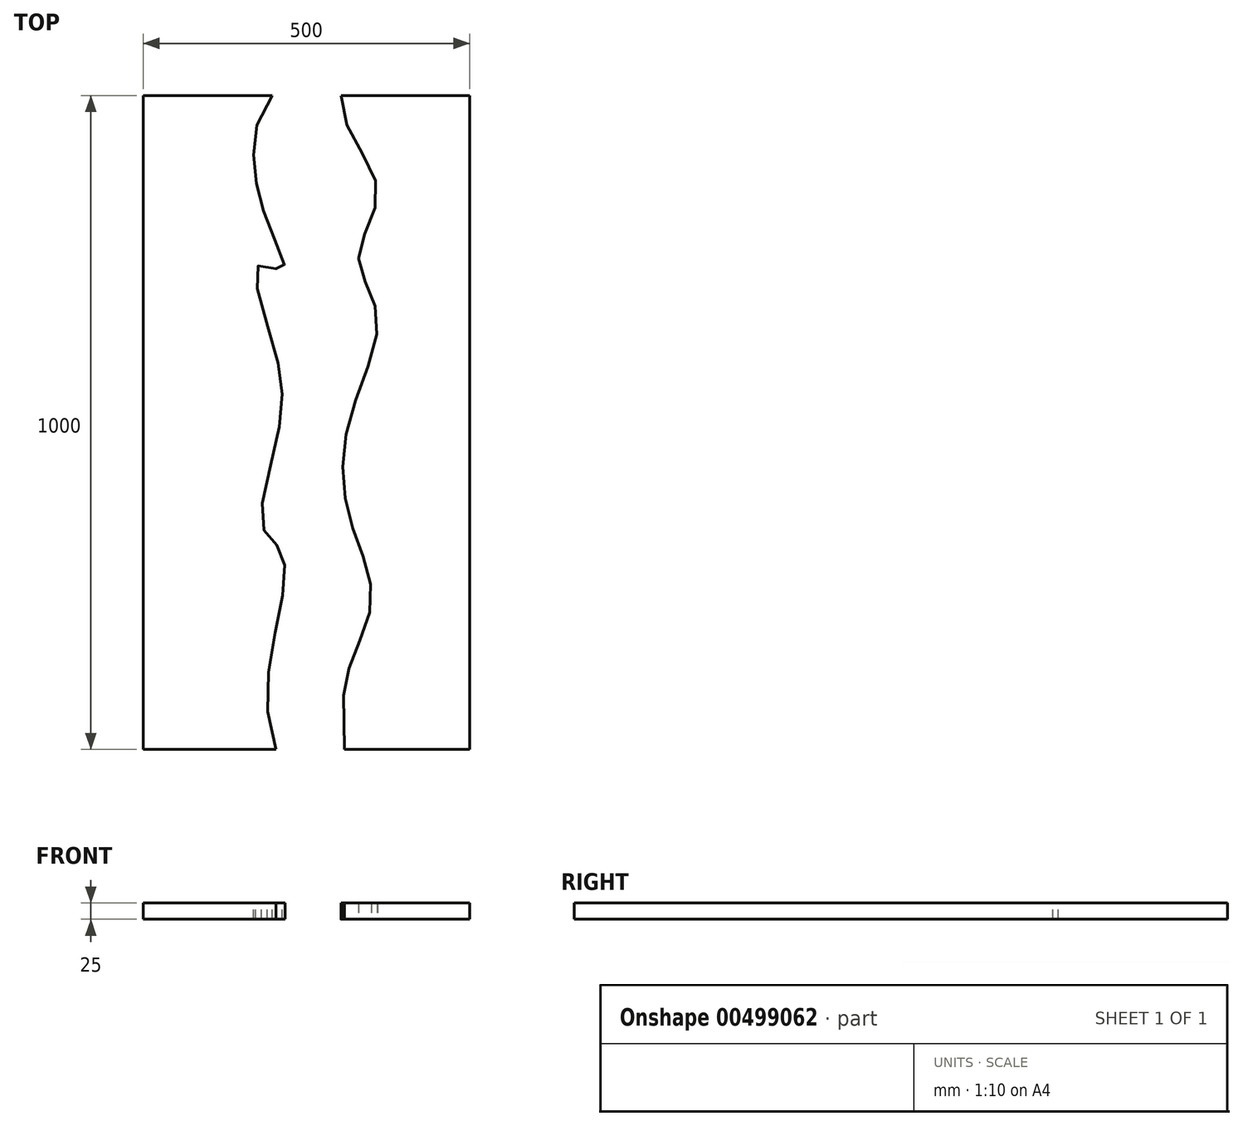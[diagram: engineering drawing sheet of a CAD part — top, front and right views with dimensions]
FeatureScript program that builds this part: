
annotation { "Feature Type Name" : "Feature", "Feature Type Description" : "" }
export const myFeature = defineFeature(function(context is Context, id is Id, definition is map)
    precondition{}
    {
        {
            var Q0;
            Q0=qCreatedBy(makeId("Top.planeOp"),FACE);
            var sketch = newSketch(context, id + "F0", { "sketchPlane" : qUnion([Q0])});
            skLineSegment(sketch, "E0.bottom", {"start": v(-249.04, 423.6) * mm, "end": v(250.96, 423.6) * mm});
            skLineSegment(sketch, "E0.top", {"start": v(-249.04, -576.4) * mm, "end": v(250.96, -576.4) * mm});
            skLineSegment(sketch, "E0.left", {"start": v(-249.04, 423.6) * mm, "end": v(-249.04, -576.4) * mm});
            skLineSegment(sketch, "E0.right", {"start": v(250.96, 423.6) * mm, "end": v(250.96, -576.4) * mm});
            skSolve(sketch);
        }
        {
            var Q0;
            Q0 = qSketchRegion(id + "F0", true);
            extrude(context, id + "F1", {"entities" : qUnion([Q0]), "depth" : 25 * mm, "offsetDistance" : 25 * mm});
        }
        {
            var Q0;
            Q0=makeQuery(id+"F1.opExtrude","CAP_FACE",FACE,{"disambiguationData":[OSD([sQuery(id+"F0.wireOp",EDGE,"E0.bottom"),sQuery(id+"F0.wireOp",EDGE,"E0.top"),sQuery(id+"F0.wireOp",EDGE,"E0.left"),sQuery(id+"F0.wireOp",EDGE,"E0.right")])],"isStart":false});
            var sketch = newSketch(context, id + "F2", { "sketchPlane" : qUnion([Q0])});
            skPoint(sketch, "E1.16.internal.snap0", {"position": v(250.96, -76.4) * mm});
            skFitSpline(sketch, "E1", {"points": [v(-51.17, 423.6) * mm, v(-78.61, 314.14) * mm, v(-53, 215.36) * mm, v(-34.71, 156.83) * mm, v(-71.3, 164.14) * mm, v(-51.17, 47.07) * mm, v(-40.2, -82.8) * mm, v(-65.8, -236.47) * mm, v(-36.54, -274.88) * mm, v(-45.69, -391.96) * mm, v(-45.69, -576.4) * mm, v(31.02, -651.88) * mm, v(59.3, -576.4) * mm, v(61.47, -469.15) * mm, v(100.63, -347.33) * mm, v(68, -225.5) * mm, v(65.82, -76.4) * mm, v(109.33, 85.57) * mm, v(81.05, 176.94) * mm, v(109.33, 279.18) * mm, v(54.95, 405.35) * mm, v(54.95, 483.66) * mm, v(-51.17, 423.6) * mm]});
            skSolve(sketch);
        }
        {
            var Q0;
            Q0 = qSketchRegion(id + "F2", true);
            extrude(context, id + "F3", {"entities" : qUnion([Q0]), "operationType" : NewBodyOperationType.REMOVE, "oppositeDirection" : true, "depth" : 99 * mm, "offsetDistance" : 25 * mm});
        }
    });
